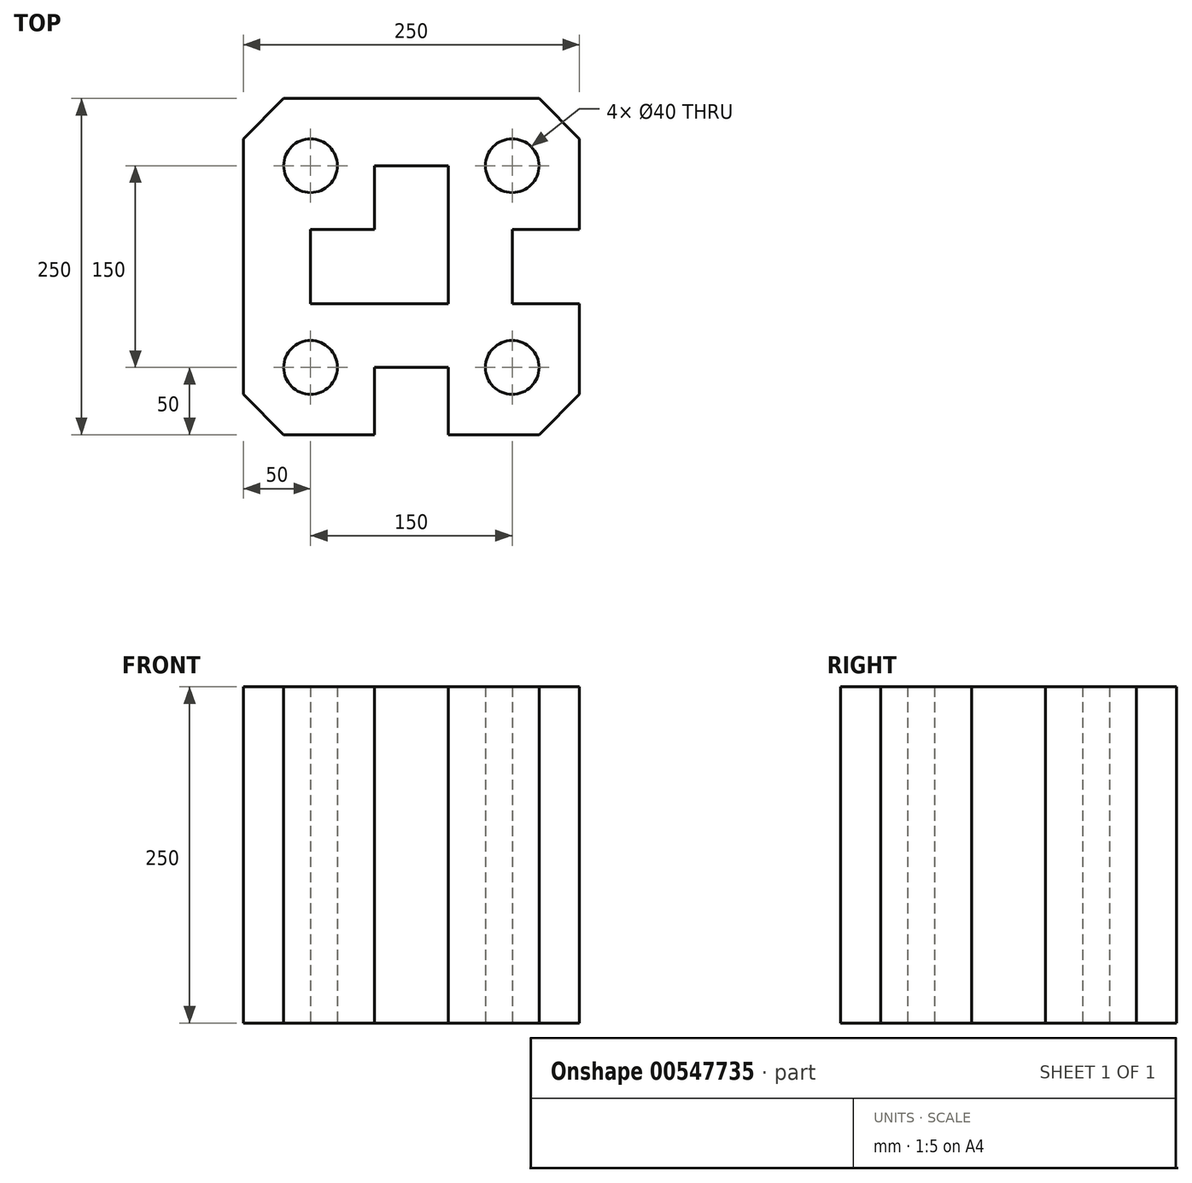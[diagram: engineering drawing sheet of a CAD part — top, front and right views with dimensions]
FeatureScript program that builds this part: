
annotation { "Feature Type Name" : "Feature", "Feature Type Description" : "" }
export const myFeature = defineFeature(function(context is Context, id is Id, definition is map)
    precondition{}
    {
        {
            var Q0;
            Q0=qCreatedBy(makeId("Top.planeOp"),FACE);
            var sketch = newSketch(context, id + "F0", { "sketchPlane" : qUnion([Q0])});
            skLineSegment(sketch, "E0.bottom", {"start": v(95, -125) * mm, "end": v(27.5, -125) * mm});
            skLineSegment(sketch, "E0.top", {"start": v(95, 125) * mm, "end": v(-95, 125) * mm});
            skLineSegment(sketch, "E0.left", {"start": v(125, -95) * mm, "end": v(125, -27.5) * mm});
            skLineSegment(sketch, "E0.right", {"start": v(-125, -95) * mm, "end": v(-125, 95) * mm});
            skPoint(sketch, "E0.middle", {"position": v(0, 0) * mm});
            skLineSegment(sketch, "E1", {"start": v(0, 0) * mm, "end": v(0, -125) * mm, "construction": true});
            skLineSegment(sketch, "E2", {"start": v(0, 0) * mm, "end": v(125, 0) * mm, "construction": true});
            skLineSegment(sketch, "E3.top", {"start": v(27.5, -75) * mm, "end": v(-27.5, -75) * mm});
            skLineSegment(sketch, "E3.left", {"start": v(27.5, -125) * mm, "end": v(27.5, -75) * mm});
            skLineSegment(sketch, "E3.right", {"start": v(-27.5, -125) * mm, "end": v(-27.5, -75) * mm});
            skPoint(sketch, "E3.middle", {"position": v(0, -100) * mm});
            skLineSegment(sketch, "E4.trimOffspring", {"start": v(-27.5, -125) * mm, "end": v(-95, -125) * mm});
            skLineSegment(sketch, "E5.bottom", {"start": v(125, 27.5) * mm, "end": v(75, 27.5) * mm});
            skLineSegment(sketch, "E5.top", {"start": v(125, -27.5) * mm, "end": v(75, -27.5) * mm});
            skLineSegment(sketch, "E5.right", {"start": v(75, 27.5) * mm, "end": v(75, -27.5) * mm});
            skPoint(sketch, "E5.middle", {"position": v(100, 0) * mm});
            skLineSegment(sketch, "E6.trimOffspring", {"start": v(125, 27.5) * mm, "end": v(125, 95) * mm});
            skLineSegment(sketch, "E7", {"start": v(-95, 125) * mm, "end": v(-125, 95) * mm});
            skLineSegment(sketch, "E8", {"start": v(-95, -125) * mm, "end": v(-125, -95) * mm});
            skLineSegment(sketch, "E9", {"start": v(125, -95) * mm, "end": v(95, -125) * mm});
            skLineSegment(sketch, "E10", {"start": v(95, 125) * mm, "end": v(125, 95) * mm});
            skPoint(sketch, "E11.orphan", {"position": v(-125, 125) * mm});
            skPoint(sketch, "E12.orphan", {"position": v(125, 125) * mm});
            skPoint(sketch, "E13.orphan", {"position": v(125, -125) * mm});
            skPoint(sketch, "E14.orphan", {"position": v(-125, -125) * mm});
            skLineSegment(sketch, "E15", {"start": v(-75, -27.5) * mm, "end": v(27.5, -27.5) * mm});
            skLineSegment(sketch, "E16", {"start": v(27.5, -27.5) * mm, "end": v(27.5, 75) * mm});
            skLineSegment(sketch, "E17", {"start": v(27.5, 75) * mm, "end": v(-27.5, 75) * mm});
            skLineSegment(sketch, "E18", {"start": v(-27.5, 75) * mm, "end": v(-27.5, 27.5) * mm});
            skLineSegment(sketch, "E19", {"start": v(-27.5, 27.5) * mm, "end": v(-75, 27.5) * mm});
            skLineSegment(sketch, "E20", {"start": v(-75, 27.5) * mm, "end": v(-75, -27.5) * mm});
            skCircle(sketch, "E21", {"center": v(-75, 75) * mm, "radius": 20 * mm});
            skCircle(sketch, "E22", {"center": v(75, 75) * mm, "radius": 20 * mm});
            skCircle(sketch, "E23", {"center": v(75, -75) * mm, "radius": 20 * mm});
            skCircle(sketch, "E24", {"center": v(-75, -75) * mm, "radius": 20 * mm});
            skSolve(sketch);
        }
        {
            var Q0;
            Q0=makeQuery(id+"F0.imprint","IMPRINT",FACE,{"disambiguationData":[TD([[makeQuery(id+"F0.imprint","IMPRINT",EDGE,{"derivedFrom":sQuery(id+"F0.wireOp",EDGE,"E0.bottom")}),-1.0]])]});
            extrude(context, id + "F1", {"entities" : qUnion([Q0]), "endBound" : BoundingType.SYMMETRIC, "depth" : 250 * mm, "offsetDistance" : 25 * mm});
        }
    });
